# Revit family: Storage-Teknion-MXCLN-Credenza-Expansion_Meeting-R2022
name_source: partatom
category: Furniture
units: mm (PartAtom-declared; Revit-internal decimal feet)

## family parameters
Always vertical = Yes
Cut with Voids When Loaded = No
Enable Cutting in Views = No
OmniClass Number = 23.40.20.00
OmniClass Title = General Furniture and Specialties
Render Appearance Source = Family Geometry
Room Calculation Point = No
Shared = Yes
Work Plane-Based = No

## types (3) — shared parameters
Assembly Code = E2020200
Manufacturer = Teknion
Manufacturer Fax = 416.661.4586
Part Number = MXCLN
Product Documentation Link = http://www.teknion.com
Product Line = Credenzas
Product Page URL = https://www.teknion.com
Series = Meeting Expansion
Sustainability Data = https://www.teknion.com
URL = www.teknion.com
Unit Weight URL = http://www.teknion.com
Warranty = http://www.teknion.com
zero-valued in all types: Default Elevation

## per-type parameters (varying)
| type | Bin 1 | Bin 2 | Description | Model |
| No Pull-Out Bin | No | No | Meeting Expansion, Credenzas - No Pull-Out Bin | MXCLN______N |
| 1 Pull-Out Bin | Yes | No | Meeting Expansion, Credenzas - 1 Pull-Out Bin | MXCLN______R / MXCLN______L |
| 2 Pull-Out Bins | Yes | Yes | Meeting Expansion, Credenzas - 2 Pull-Out Bins | MXCLN______T / MXCLN______V |

type visibility flags: 3 boolean params named "<type name>" — each type sets only its own to Yes (folded from table)

## geometry (parser evidence)
native form markers: Sweep x4
no freeform markers — native parametric forms only
